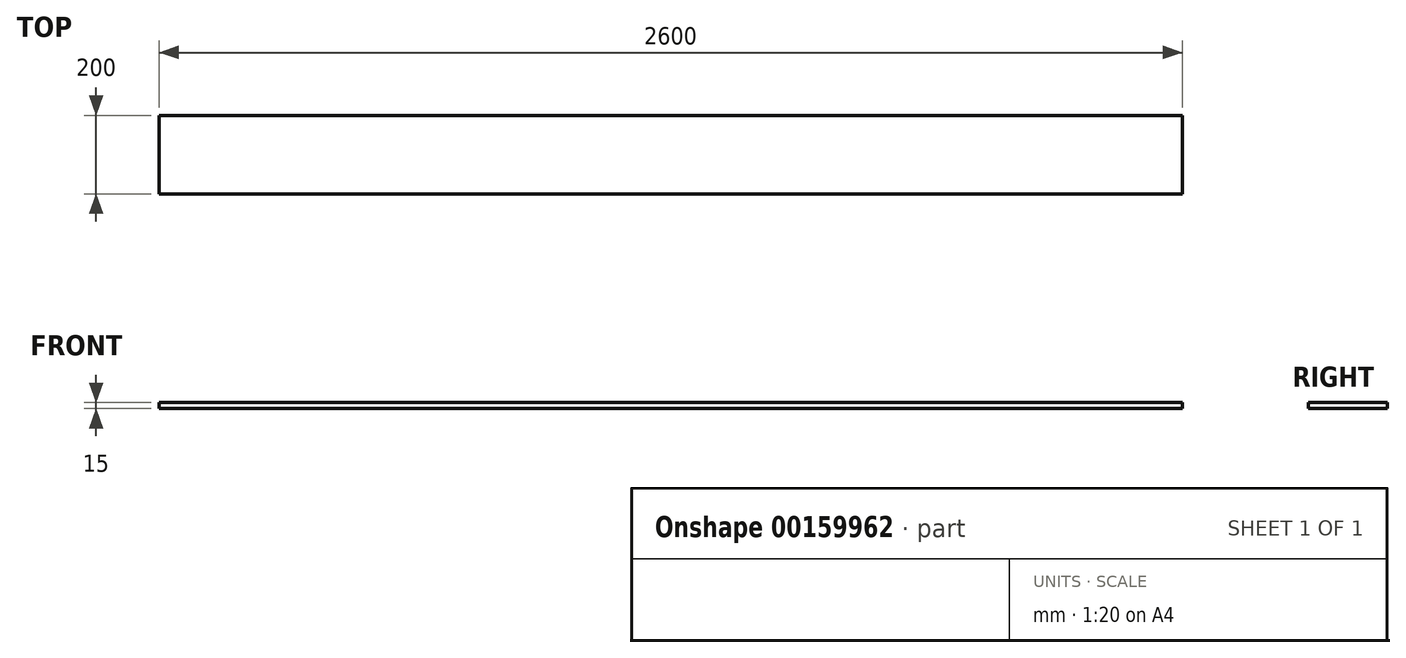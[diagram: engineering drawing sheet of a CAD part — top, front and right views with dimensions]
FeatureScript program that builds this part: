
annotation { "Feature Type Name" : "Feature", "Feature Type Description" : "" }
export const myFeature = defineFeature(function(context is Context, id is Id, definition is map)
    precondition{}
    {
        {
            var Q0;
            Q0=qCreatedBy(makeId("Top.planeOp"),FACE);
            var sketch = newSketch(context, id + "F0", { "sketchPlane" : qUnion([Q0])});
            skLineSegment(sketch, "E0.bottom", {"start": v(-248.5, 90.92) * mm, "end": v(2351.5, 90.92) * mm});
            skLineSegment(sketch, "E0.top", {"start": v(-248.5, -109.08) * mm, "end": v(2351.5, -109.08) * mm});
            skLineSegment(sketch, "E0.left", {"start": v(-248.5, 90.92) * mm, "end": v(-248.5, -109.08) * mm});
            skLineSegment(sketch, "E0.right", {"start": v(2351.5, 90.92) * mm, "end": v(2351.5, -109.08) * mm});
            skSolve(sketch);
        }
        {
            var Q0;
            Q0=makeQuery(id+"F0.imprint","IMPRINT",FACE,{"disambiguationData":[TD([[makeQuery(id+"F0.imprint","IMPRINT",EDGE,{"derivedFrom":sQuery(id+"F0.wireOp",EDGE,"E0.bottom")}),-1.0]])]});
            extrude(context, id + "F1", {"entities" : qUnion([Q0]), "depth" : 15 * mm});
        }
    });
